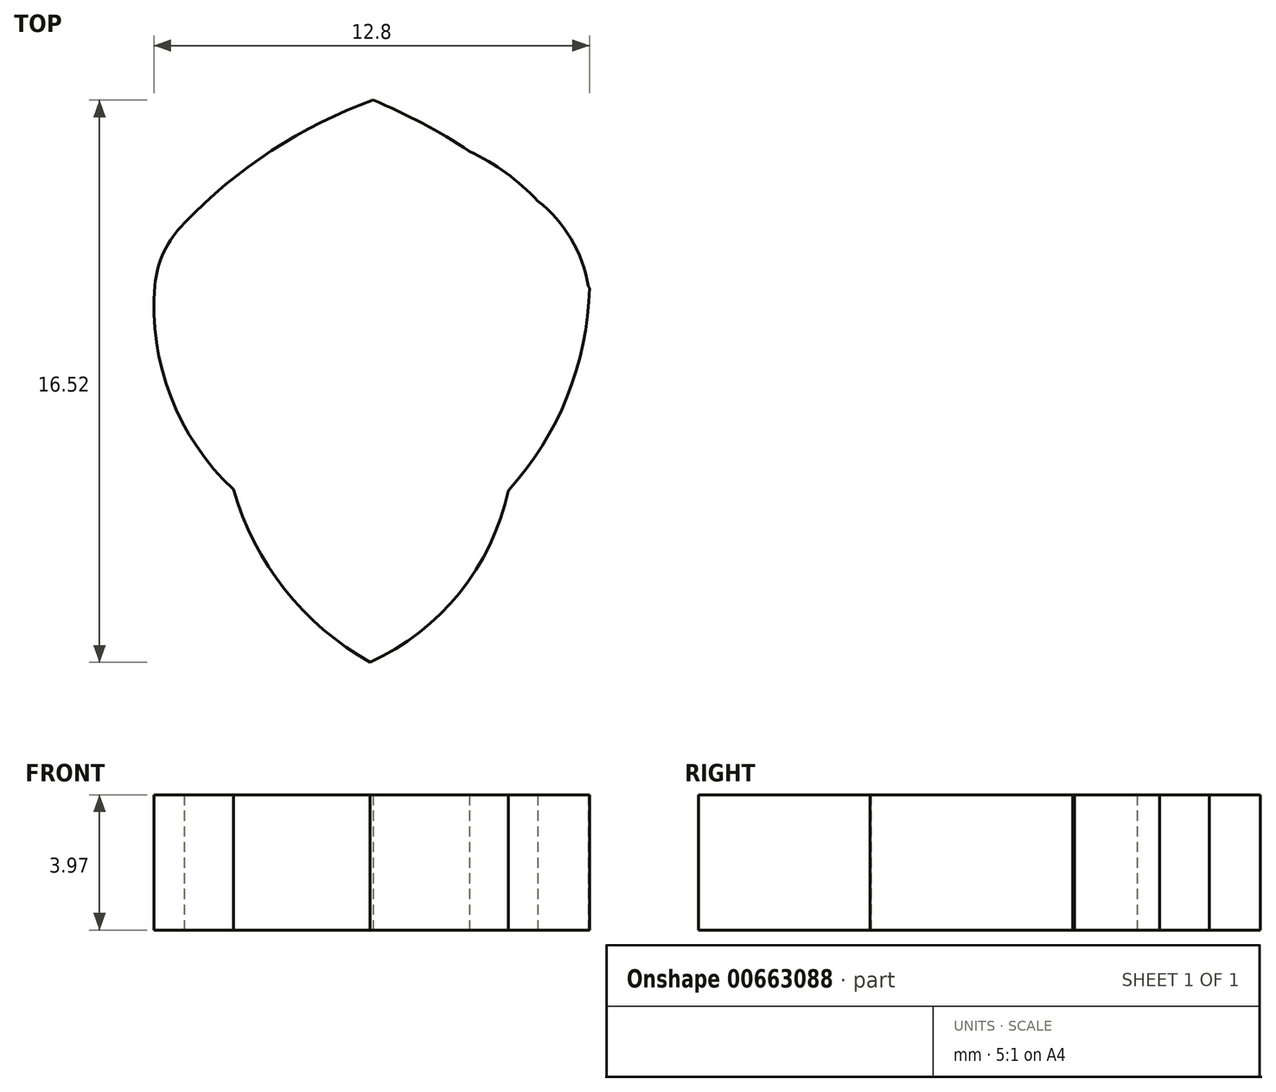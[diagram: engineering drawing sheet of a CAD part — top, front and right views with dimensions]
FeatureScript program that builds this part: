
annotation { "Feature Type Name" : "Feature", "Feature Type Description" : "" }
export const myFeature = defineFeature(function(context is Context, id is Id, definition is map)
    precondition{}
    {
        {
            var Q0;
            Q0=qCreatedBy(makeId("Top.planeOp"),FACE);
            var sketch = newSketch(context, id + "F0", { "sketchPlane" : qUnion([Q0])});
            skPoint(sketch, "E0.center", {"position": v(0, 0) * mm});
            skLineSegment(sketch, "E1", {"start": v(-12.37, 4.64) * mm, "end": v(-12.37, 4.57) * mm});
            skArc(sketch, "E2", {"start": v(4.84, 6.15) * mm, "mid": v(3.9, 6.98) * mm, "end": v(2.84, 7.61) * mm});
            skArc(sketch, "E3", {"start": v(6.33, 3.65) * mm, "mid": v(5.82, 5.04) * mm, "end": v(4.84, 6.15) * mm});
            skArc(sketch, "E4.trimOffspring", {"start": v(2.84, 7.61) * mm, "mid": v(1.46, 8.44) * mm, "end": v(0, 9.12) * mm});
            skLineSegment(sketch, "E5", {"start": v(7.76, 1.05) * mm, "end": v(7.76, 1.05) * mm});
            skLineSegment(sketch, "E6", {"start": v(8, -1.42) * mm, "end": v(8, -1.42) * mm});
            skLineSegment(sketch, "E7", {"start": v(6.33, 3.65) * mm, "end": v(6.36, 3.6) * mm});
            skArc(sketch, "E8", {"start": v(-5.55, 5.5) * mm, "mid": v(-6.15, 4.66) * mm, "end": v(-6.41, 3.67) * mm});
            skArc(sketch, "E9", {"start": v(0, 9.12) * mm, "mid": v(-2.98, 7.63) * mm, "end": v(-5.55, 5.5) * mm});
            skArc(sketch, "E10", {"start": v(-0.1, -7.4) * mm, "mid": v(2.54, -5.36) * mm, "end": v(3.97, -2.35) * mm});
            skArc(sketch, "E11", {"start": v(3.97, -2.35) * mm, "mid": v(5.7, 0.4) * mm, "end": v(6.36, 3.6) * mm});
            skArc(sketch, "E12", {"start": v(-6.41, 3.67) * mm, "mid": v(-5.95, 0.4) * mm, "end": v(-4.1, -2.33) * mm});
            skArc(sketch, "E13", {"start": v(-4.1, -2.33) * mm, "mid": v(-2.6, -5.26) * mm, "end": v(-0.1, -7.4) * mm});
            skSolve(sketch);
        }
        {
            var Q0;
            Q0=makeQuery(id+"F0.imprint","IMPRINT",FACE,{"disambiguationData":[TD([[makeQuery(id+"F0.imprint","IMPRINT",EDGE,{"derivedFrom":sQuery(id+"F0.wireOp",EDGE,"E2")}),1.0]])]});
            extrude(context, id + "F1", {"entities" : qUnion([Q0]), "depth" : 3.97 * mm, "offsetDistance" : 25.4 * mm});
        }
    });
